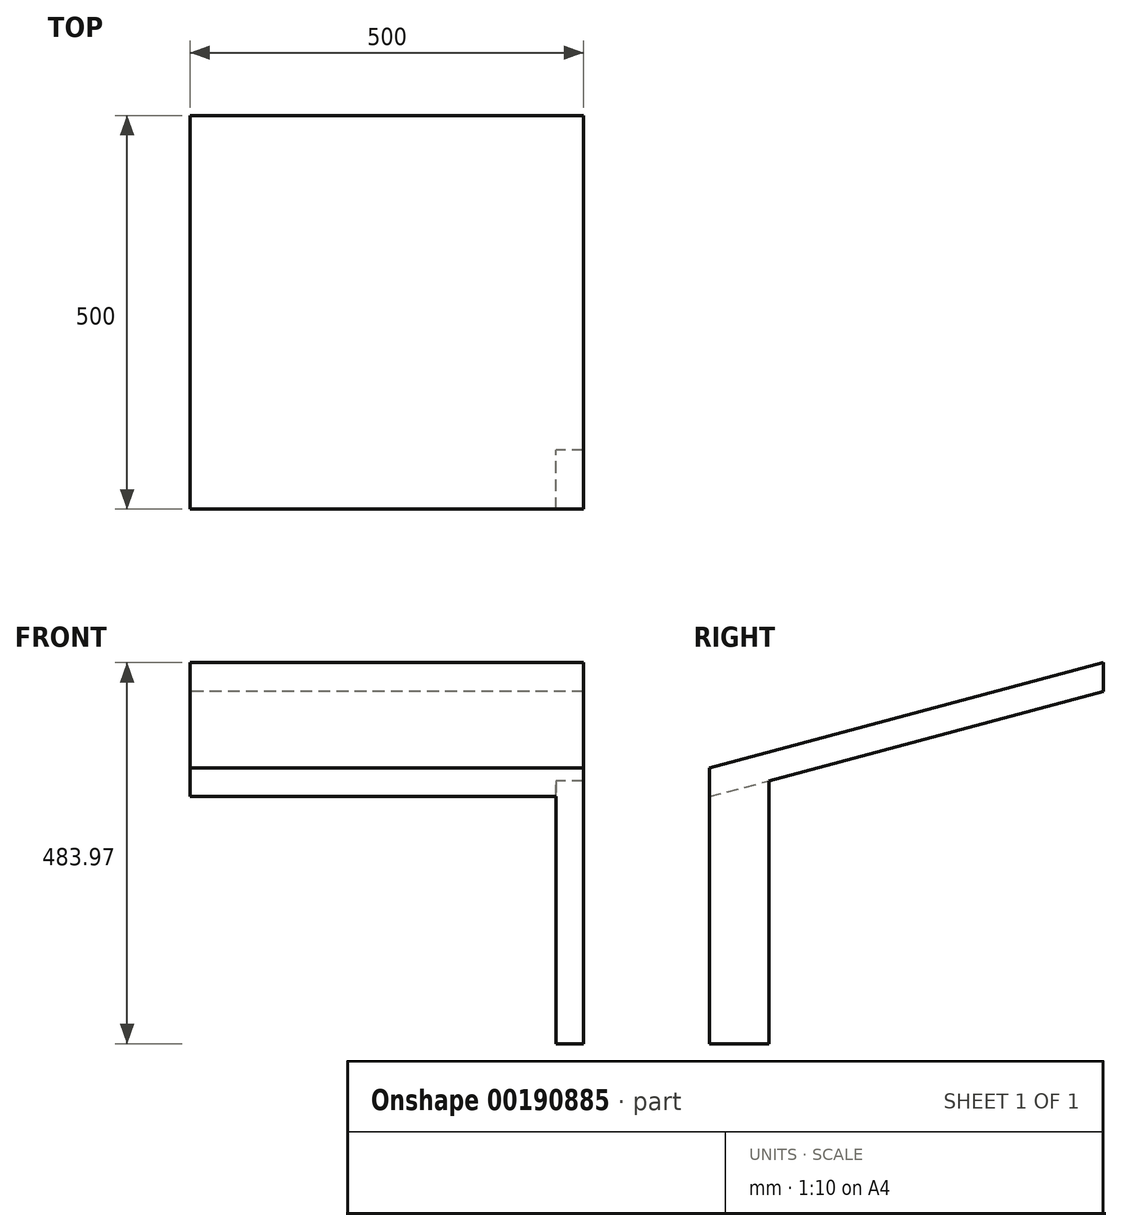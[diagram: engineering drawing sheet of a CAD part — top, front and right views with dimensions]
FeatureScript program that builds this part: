
annotation { "Feature Type Name" : "Feature", "Feature Type Description" : "" }
export const myFeature = defineFeature(function(context is Context, id is Id, definition is map)
    precondition{}
    {
        {
            var Q0;
            Q0=qCreatedBy(makeId("Right.planeOp"),FACE);
            var sketch = newSketch(context, id + "F0", { "sketchPlane" : qUnion([Q0])});
            skLineSegment(sketch, "E0", {"start": v(-1000, 0) * mm, "end": v(0, 0) * mm});
            skLineSegment(sketch, "E1", {"start": v(0, 0) * mm, "end": v(0, 1000) * mm});
            skLineSegment(sketch, "E2", {"start": v(-500, 0) * mm, "end": v(-500, 350) * mm});
            skLineSegment(sketch, "E3", {"start": v(-500, 350) * mm, "end": v(0, 483.97) * mm});
            skLineSegment(sketch, "E4", {"start": v(-425, 0) * mm, "end": v(-425, 333.86) * mm});
            skLineSegment(sketch, "E5", {"start": v(-425, 333.86) * mm, "end": v(0, 447.74) * mm});
            skSolve(sketch);
        }
        {
            var Q0;
            Q0=sQuery(id+"F0.wireOp",EDGE,"E1");
            var Q1;
            Q1=sQuery(id+"F0.wireOp",EDGE,"E0");
            extrude(context, id + "F1", {"bodyType" : ToolBodyType.SURFACE, "surfaceEntities" : qUnion([Q0, Q1]), "depth" : 1500 * mm, "symmetric" : true});
        }
        {
            var Q0;
            Q0=qCreatedBy(makeId("Right.planeOp"),FACE);
            var sketch = newSketch(context, id + "F2", { "sketchPlane" : qUnion([Q0])});
            skLineSegment(sketch, "E6.0", {"start": v(0, 447.74) * mm, "end": v(0, 483.97) * mm});
            skLineSegment(sketch, "E6.1", {"start": v(-500, 313.77) * mm, "end": v(0, 447.74) * mm});
            skLineSegment(sketch, "E6.2", {"start": v(-500, 350) * mm, "end": v(0, 483.97) * mm});
            skLineSegment(sketch, "E6.3", {"start": v(-500, 313.77) * mm, "end": v(-500, 350) * mm});
            skSolve(sketch);
        }
        {
            var Q0;
            Q0 = qSketchRegion(id + "F2", true);
            extrude(context, id + "F3", {"entities" : qUnion([Q0]), "depth" : 500 * mm, "symmetric" : true});
        }
        {
            var Q0;
            Q0=qCreatedBy(makeId("Top.planeOp"),FACE);
            var sketch = newSketch(context, id + "F4", { "sketchPlane" : qUnion([Q0])});
            skLineSegment(sketch, "E7.bottom", {"start": v(250, -500) * mm, "end": v(215, -500) * mm});
            skLineSegment(sketch, "E7.top", {"start": v(250, -425) * mm, "end": v(215, -425) * mm});
            skLineSegment(sketch, "E7.left", {"start": v(250, -500) * mm, "end": v(250, -425) * mm});
            skLineSegment(sketch, "E7.right", {"start": v(215, -500) * mm, "end": v(215, -425) * mm});
            skSolve(sketch);
        }
        {
            var Q0;
            Q0 = qSketchRegion(id + "F4", true);
            extrude(context, id + "F5", {"entities" : qUnion([Q0]), "operationType" : NewBodyOperationType.ADD, "endBound" : BoundingType.UP_TO_NEXT, "depth" : 25 * mm});
        }
    });
